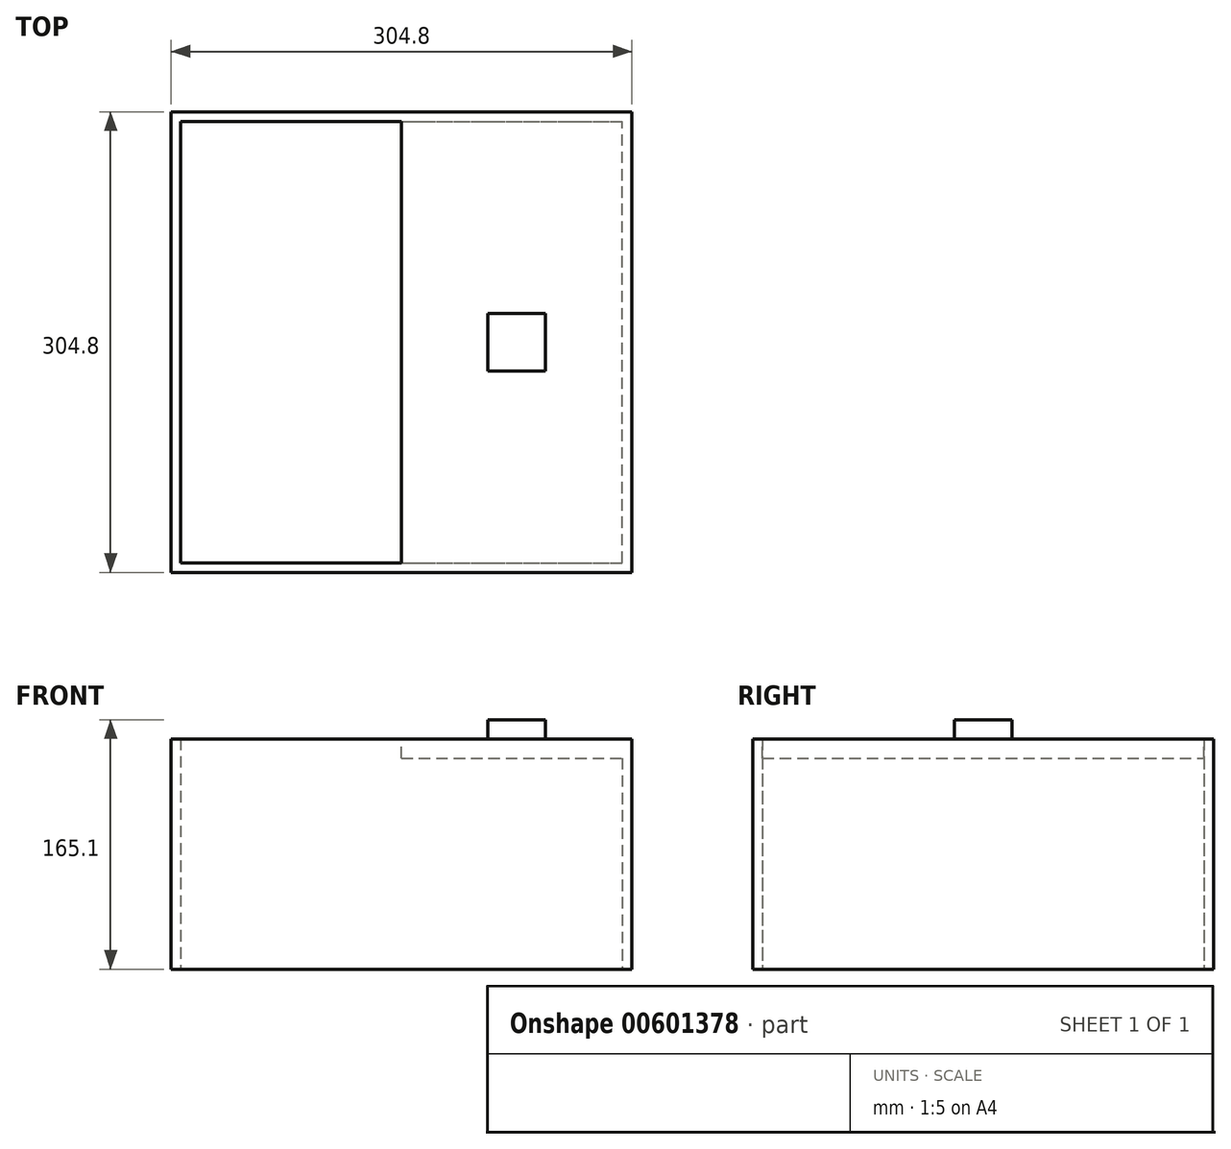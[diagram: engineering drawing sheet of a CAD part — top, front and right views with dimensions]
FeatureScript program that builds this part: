
annotation { "Feature Type Name" : "Feature", "Feature Type Description" : "" }
export const myFeature = defineFeature(function(context is Context, id is Id, definition is map)
    precondition{}
    {
        {
            var Q0;
            Q0=qCreatedBy(makeId("Front.planeOp"),FACE);
            var sketch = newSketch(context, id + "F0", { "sketchPlane" : qUnion([Q0])});
            skLineSegment(sketch, "E0.bottom", {"start": v(-148.43, 59.27) * mm, "end": v(156.37, 59.27) * mm});
            skLineSegment(sketch, "E0.top", {"start": v(-148.43, -93.13) * mm, "end": v(156.37, -93.13) * mm});
            skLineSegment(sketch, "E0.left", {"start": v(-148.43, 59.27) * mm, "end": v(-148.43, -93.13) * mm});
            skLineSegment(sketch, "E0.right", {"start": v(156.37, 59.27) * mm, "end": v(156.37, -93.13) * mm});
            skSolve(sketch);
        }
        {
            var Q0;
            Q0 = qSketchRegion(id + "F0", true);
            extrude(context, id + "F1", {"entities" : qUnion([Q0]), "endBound" : BoundingType.SYMMETRIC, "depth" : 304.8 * mm, "offsetDistance" : 25.4 * mm});
        }
        {
            var Q0;
            Q0=makeQuery(id+"F1.opExtrude","SWEPT_FACE",FACE,{"disambiguationData":[OSD([sQuery(id+"F0.wireOp",EDGE,"E0.top")])]});
            var sketch = newSketch(context, id + "F2", { "sketchPlane" : qUnion([Q0])});
            skLineSegment(sketch, "E1.bottom", {"start": v(-142.08, 146.05) * mm, "end": v(150.02, 146.05) * mm});
            skLineSegment(sketch, "E1.top", {"start": v(-142.08, -146.05) * mm, "end": v(150.02, -146.05) * mm});
            skLineSegment(sketch, "E1.left", {"start": v(-142.08, 146.05) * mm, "end": v(-142.08, -146.05) * mm});
            skLineSegment(sketch, "E1.right", {"start": v(150.02, 146.05) * mm, "end": v(150.02, -146.05) * mm});
            skPoint(sketch, "E2", {"position": v(3.97, 152.4) * mm});
            skPoint(sketch, "E3", {"position": v(3.97, -152.4) * mm});
            skPoint(sketch, "E4", {"position": v(-148.43, 0) * mm});
            skPoint(sketch, "E5", {"position": v(-142.08, 0) * mm});
            skPoint(sketch, "E6.positionSnap0", {"position": v(3.97, 146.05) * mm});
            skSolve(sketch);
        }
        {
            var Q0;
            Q0 = qSketchRegion(id + "F2", true);
            extrude(context, id + "F3", {"entities" : qUnion([Q0]), "operationType" : NewBodyOperationType.REMOVE, "oppositeDirection" : true, "depth" : 139.7 * mm, "offsetDistance" : 25.4 * mm});
        }
        {
            var Q0;
            Q0=makeQuery(id+"F1.opExtrude","SWEPT_FACE",FACE,{"disambiguationData":[OSD([sQuery(id+"F0.wireOp",EDGE,"E0.bottom")])]});
            var sketch = newSketch(context, id + "F4", { "sketchPlane" : qUnion([Q0])});
            skLineSegment(sketch, "E7.bottom", {"start": v(-148.43, 152.4) * mm, "end": v(3.97, 152.4) * mm});
            skLineSegment(sketch, "E7.top", {"start": v(-148.43, -152.4) * mm, "end": v(3.97, -152.4) * mm});
            skLineSegment(sketch, "E7.left", {"start": v(-148.43, 152.4) * mm, "end": v(-148.43, -152.4) * mm});
            skLineSegment(sketch, "E7.right", {"start": v(3.97, 152.4) * mm, "end": v(3.97, -152.4) * mm});
            skLineSegment(sketch, "E8.bottom", {"start": v(-142.08, 146.05) * mm, "end": v(3.97, 146.05) * mm});
            skLineSegment(sketch, "E8.top", {"start": v(-142.08, -146.05) * mm, "end": v(3.97, -146.05) * mm});
            skLineSegment(sketch, "E8.left", {"start": v(-142.08, 146.05) * mm, "end": v(-142.08, -146.05) * mm});
            skLineSegment(sketch, "E8.right", {"start": v(3.97, 146.05) * mm, "end": v(3.97, -146.05) * mm});
            skPoint(sketch, "E9", {"position": v(-142.08, 0) * mm});
            skLineSegment(sketch, "E10", {"start": v(3.97, 0) * mm, "end": v(156.37, 0) * mm});
            skPoint(sketch, "E11", {"position": v(80.17, 0) * mm});
            skLineSegment(sketch, "E12.bottom", {"start": v(61.12, 19.05) * mm, "end": v(99.22, 19.05) * mm});
            skLineSegment(sketch, "E12.top", {"start": v(61.12, -19.05) * mm, "end": v(99.22, -19.05) * mm});
            skLineSegment(sketch, "E12.left", {"start": v(61.12, 19.05) * mm, "end": v(61.12, -19.05) * mm});
            skLineSegment(sketch, "E12.right", {"start": v(99.22, 19.05) * mm, "end": v(99.22, -19.05) * mm});
            skPoint(sketch, "E13", {"position": v(80.17, 19.05) * mm});
            skPoint(sketch, "E14", {"position": v(61.12, 0) * mm});
            skSolve(sketch);
        }
        {
            var Q0;
            Q0=makeQuery(id+"F4.imprint","IMPRINT",FACE,{"disambiguationData":[TD([[makeQuery(id+"F4.imprint","IMPRINT",EDGE,{"derivedFrom":sQuery(id+"F4.wireOp",EDGE,"E8.bottom")}),-1.0]])]});
            extrude(context, id + "F5", {"entities" : qUnion([Q0]), "operationType" : NewBodyOperationType.REMOVE, "oppositeDirection" : true, "depth" : 12.7 * mm, "offsetDistance" : 25.4 * mm});
        }
        {
            var Q0;
            {var subQ5=sQuery(id+"F4.wireOp",EDGE,"E12.bottom");Q0=makeQuery(id+"F4.imprint","IMPRINT",FACE,{"disambiguationData":[TD([[makeQuery(id+"F4.imprint","IMPRINT",EDGE,{"derivedFrom":subQ5}),-1.0]])]});}
            var Q1;
            {var subQ5=sQuery(id+"F4.wireOp",EDGE,"E12.top");Q1=makeQuery(id+"F4.imprint","IMPRINT",FACE,{"disambiguationData":[TD([[makeQuery(id+"F4.imprint","IMPRINT",EDGE,{"derivedFrom":subQ5}),1.0]])]});}
            extrude(context, id + "F6", {"entities" : qUnion([Q0, Q1]), "operationType" : NewBodyOperationType.ADD, "depth" : 12.7 * mm, "offsetDistance" : 25.4 * mm});
        }
    });
